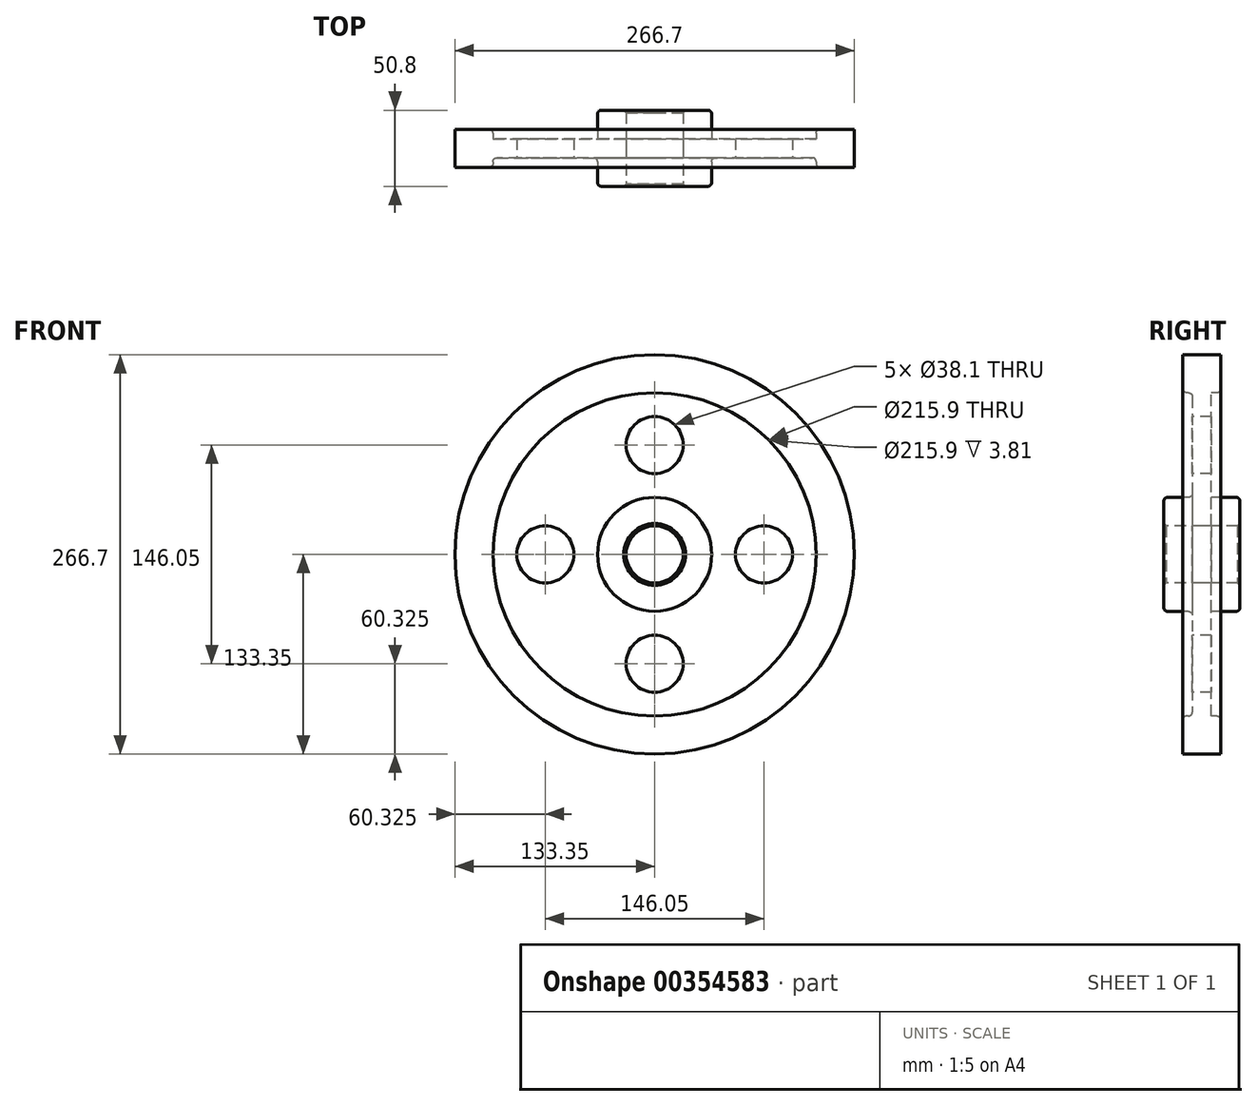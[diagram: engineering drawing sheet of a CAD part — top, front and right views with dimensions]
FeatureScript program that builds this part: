
annotation { "Feature Type Name" : "Feature", "Feature Type Description" : "" }
export const myFeature = defineFeature(function(context is Context, id is Id, definition is map)
    precondition{}
    {
        {
            var Q0;
            Q0=qCreatedBy(makeId("Right.planeOp"),FACE);
            var sketch = newSketch(context, id + "F0", { "sketchPlane" : qUnion([Q0])});
            skLineSegment(sketch, "E0", {"start": v(0, 0) * mm, "end": v(99.39, 0) * mm, "construction": true});
            skLineSegment(sketch, "E1.0", {"start": v(0, 19.05) * mm, "end": v(25.4, 19.05) * mm});
            skLineSegment(sketch, "E2.0", {"start": v(6.35, 38.1) * mm, "end": v(25.4, 38.1) * mm});
            skLineSegment(sketch, "E3.0", {"start": v(6.35, 107.95) * mm, "end": v(12.7, 107.95) * mm});
            skLineSegment(sketch, "E4.0", {"start": v(0, 133.35) * mm, "end": v(12.7, 133.35) * mm});
            skLineSegment(sketch, "E5", {"start": v(0, 133.35) * mm, "end": v(0, 0) * mm});
            skLineSegment(sketch, "E6.0", {"start": v(25.4, 38.1) * mm, "end": v(25.4, 19.05) * mm});
            skLineSegment(sketch, "E7.0", {"start": v(12.7, 133.35) * mm, "end": v(12.7, 107.95) * mm});
            skLineSegment(sketch, "E8.0", {"start": v(6.35, 107.95) * mm, "end": v(6.35, 38.1) * mm});
            skLineSegment(sketch, "E9.MirrorCS", {"start": v(0, 133.35) * mm, "end": v(-12.7, 133.35) * mm});
            skLineSegment(sketch, "E10.MirrorCS", {"start": v(-12.7, 133.35) * mm, "end": v(-12.7, 107.95) * mm});
            skLineSegment(sketch, "E11.MirrorCS", {"start": v(-6.35, 107.95) * mm, "end": v(-6.35, 38.1) * mm});
            skLineSegment(sketch, "E12.MirrorCS", {"start": v(-6.35, 38.1) * mm, "end": v(-25.4, 38.1) * mm});
            skLineSegment(sketch, "E13.MirrorCS", {"start": v(-25.4, 38.1) * mm, "end": v(-25.4, 19.05) * mm});
            skLineSegment(sketch, "E14.MirrorCS", {"start": v(0, 19.05) * mm, "end": v(-25.4, 19.05) * mm});
            skLineSegment(sketch, "E15.MirrorCS", {"start": v(-6.35, 107.95) * mm, "end": v(-12.7, 107.95) * mm});
            skSolve(sketch);
        }
        {
            var Q0;
            {var subQ1=sQuery(id+"F0.wireOp",EDGE,"E1.0");Q0=makeQuery(id+"F0.imprint","IMPRINT",FACE,{"disambiguationData":[TD([[makeQuery(id+"F0.imprint","IMPRINT",EDGE,{"derivedFrom":subQ1}),1.0]])]});}
            var Q1;
            {var subQ0=sQuery(id+"F0.wireOp",EDGE,"E9.MirrorCS");Q1=makeQuery(id+"F0.imprint","IMPRINT",FACE,{"disambiguationData":[TD([[makeQuery(id+"F0.imprint","IMPRINT",EDGE,{"derivedFrom":subQ0}),1.0]])]});}
            var Q2;
            Q2=sQuery(id+"F0.wireOp",EDGE,"E0");
            revolve(context, id + "F1", {"entities" : qUnion([Q0, Q1]), "axis" : qUnion([Q2]), "revolveType" : RevolveType.FULL});
        }
        {
            var Q0;
            Q0=makeQuery(id+"F1.opRevolve","SWEPT_FACE",FACE,{"disambiguationData":[OSD([sQuery(id+"F0.wireOp",EDGE,"E11.MirrorCS")])]});
            var sketch = newSketch(context, id + "F2", { "sketchPlane" : qUnion([Q0])});
            skLineSegment(sketch, "E16", {"start": v(0, 0) * mm, "end": v(0, 73.03) * mm});
            skCircle(sketch, "E17", {"center": v(0, 73.03) * mm, "radius": 19.05 * mm});
            skCircle(sketch, "E18.1.0", {"center": v(-73.03, 0) * mm, "radius": 19.05 * mm});
            skCircle(sketch, "E18.2.0", {"center": v(0, -73.03) * mm, "radius": 19.05 * mm});
            skCircle(sketch, "E18.3.0", {"center": v(73.03, 0) * mm, "radius": 19.05 * mm});
            skPoint(sketch, "E18.center", {"position": v(0, 0) * mm});
            skSolve(sketch);
        }
        {
            var Q0;
            Q0=makeQuery(id+"F2.imprint","IMPRINT",FACE,{"disambiguationData":[TD([[makeQuery(id+"F2.imprint","IMPRINT",EDGE,{"derivedFrom":sQuery(id+"F2.wireOp",EDGE,"E18.1.0")}),1.0]])]});
            var Q1;
            Q1=makeQuery(id+"F2.imprint","IMPRINT",FACE,{"disambiguationData":[TD([[makeQuery(id+"F2.imprint","IMPRINT",EDGE,{"derivedFrom":sQuery(id+"F2.wireOp",EDGE,"E17")}),1.0]])]});
            var Q2;
            Q2=makeQuery(id+"F2.imprint","IMPRINT",FACE,{"disambiguationData":[TD([[makeQuery(id+"F2.imprint","IMPRINT",EDGE,{"derivedFrom":sQuery(id+"F2.wireOp",EDGE,"E18.3.0")}),1.0]])]});
            var Q3;
            Q3=makeQuery(id+"F2.imprint","IMPRINT",FACE,{"disambiguationData":[TD([[makeQuery(id+"F2.imprint","IMPRINT",EDGE,{"derivedFrom":sQuery(id+"F2.wireOp",EDGE,"E18.2.0")}),1.0]])]});
            extrude(context, id + "F3", {"entities" : qUnion([Q0, Q1, Q2, Q3]), "operationType" : NewBodyOperationType.REMOVE, "oppositeDirection" : true, "depth" : 25.4 * mm});
        }
        {
            var Q0;
            Q0=makeQuery(id+"F1.opRevolve","SWEPT_EDGE",EDGE,{"disambiguationData":[OSD([sQuery(id+"F0.wireOp",EDGE,"E11.MirrorCS"),sQuery(id+"F0.wireOp",EDGE,"E15.MirrorCS")])]});
            var Q1;
            Q1=makeQuery(id+"F1.opRevolve","SWEPT_EDGE",EDGE,{"disambiguationData":[OSD([sQuery(id+"F0.wireOp",EDGE,"E10.MirrorCS"),sQuery(id+"F0.wireOp",EDGE,"E15.MirrorCS")])]});
            var Q2;
            Q2=makeQuery(id+"F1.opRevolve","SWEPT_EDGE",EDGE,{"disambiguationData":[OSD([sQuery(id+"F0.wireOp",EDGE,"E12.MirrorCS"),sQuery(id+"F0.wireOp",EDGE,"E13.MirrorCS")])]});
            var Q3;
            Q3=makeQuery(id+"F1.opRevolve","SWEPT_EDGE",EDGE,{"disambiguationData":[OSD([sQuery(id+"F0.wireOp",EDGE,"E11.MirrorCS"),sQuery(id+"F0.wireOp",EDGE,"E12.MirrorCS")])]});
            var Q4;
            Q4=makeQuery(id+"F1.opRevolve","SWEPT_EDGE",EDGE,{"disambiguationData":[OSD([sQuery(id+"F0.wireOp",EDGE,"E2.0"),sQuery(id+"F0.wireOp",EDGE,"E6.0")])]});
            var Q5;
            Q5=makeQuery(id+"F1.opRevolve","SWEPT_EDGE",EDGE,{"disambiguationData":[OSD([sQuery(id+"F0.wireOp",EDGE,"E3.0"),sQuery(id+"F0.wireOp",EDGE,"E7.0")])]});
            fillet(context, id + "F4", {"entities" : qUnion([Q0, Q1, Q2, Q3, Q4, Q5]), "radius" : 2.54 * mm, "tangentPropagation" : true, "allowEdgeOverflow" : false});
        }
        {
            var Q0;
            Q0=makeQuery(id+"F1.opRevolve","SWEPT_EDGE",EDGE,{"disambiguationData":[OSD([sQuery(id+"F0.wireOp",EDGE,"E13.MirrorCS"),sQuery(id+"F0.wireOp",EDGE,"E14.MirrorCS")])]});
            var Q1;
            Q1=makeQuery(id+"F1.opRevolve","SWEPT_EDGE",EDGE,{"disambiguationData":[OSD([sQuery(id+"F0.wireOp",EDGE,"E1.0"),sQuery(id+"F0.wireOp",EDGE,"E6.0")])]});
            chamfer(context, id + "F5", {"entities" : qUnion([Q0, Q1]), "width" : 1.59 * mm, "tangentPropagation" : true});
        }
    });
